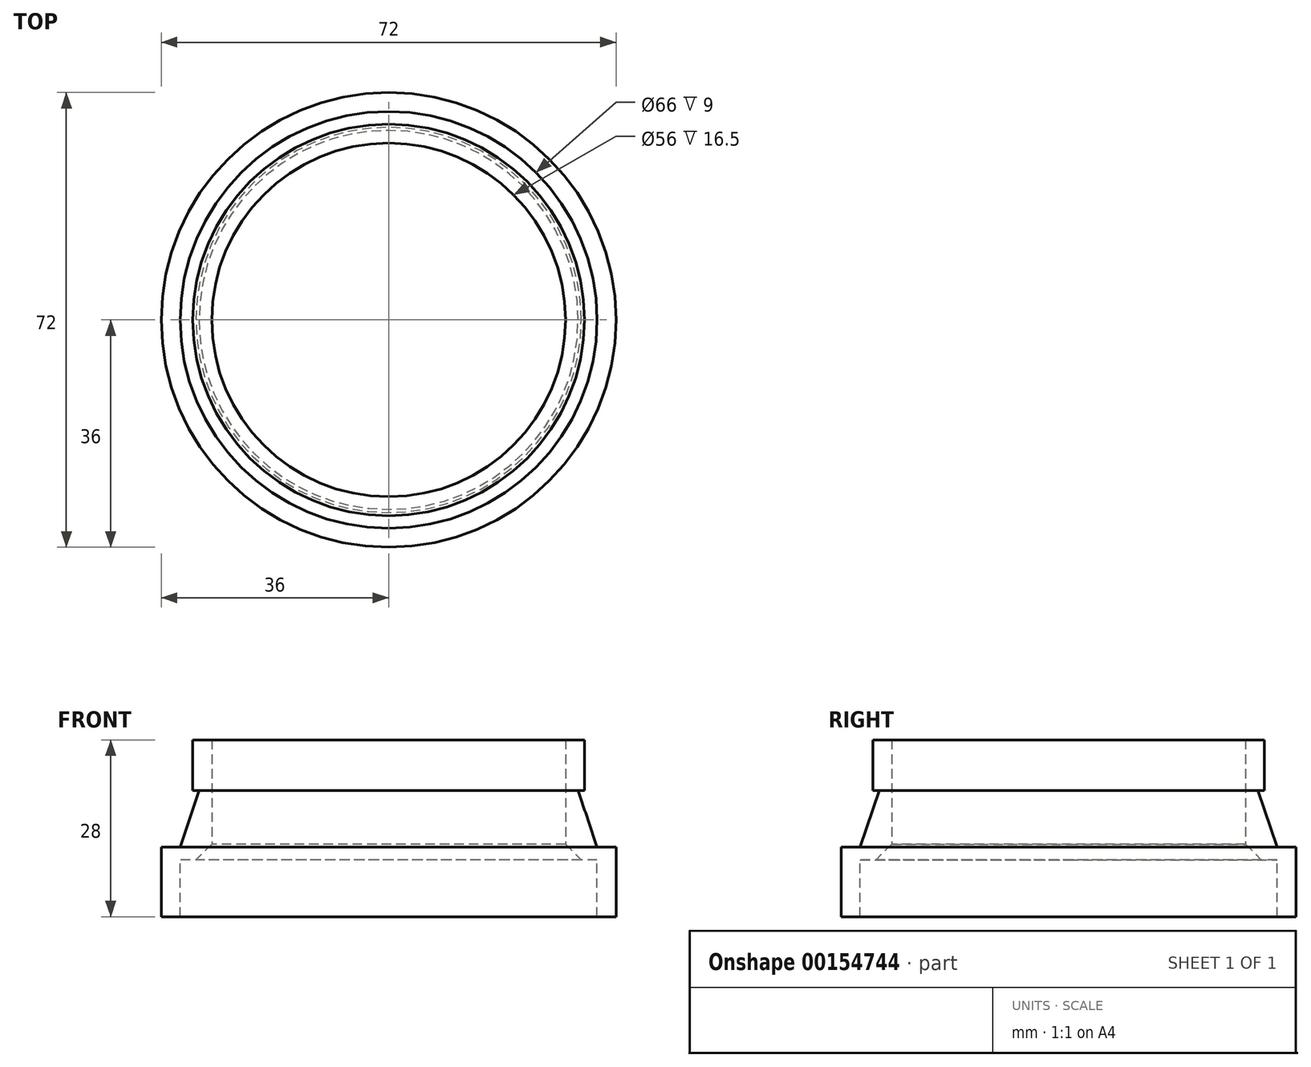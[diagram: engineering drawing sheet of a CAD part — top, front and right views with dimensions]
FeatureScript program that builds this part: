
annotation { "Feature Type Name" : "Feature", "Feature Type Description" : "" }
export const myFeature = defineFeature(function(context is Context, id is Id, definition is map)
    precondition{}
    {
        {
            var Q0;
            Q0=qCreatedBy(makeId("Top.planeOp"),FACE);
            var sketch = newSketch(context, id + "F0", { "sketchPlane" : qUnion([Q0])});
            skCircle(sketch, "E0", {"center": v(0, 0) * mm, "radius": 36 * mm});
            skCircle(sketch, "E1", {"center": v(0, 0) * mm, "radius": 28 * mm});
            skSolve(sketch);
        }
        {
            var Q0;
            Q0=makeQuery(id+"F0.imprint","IMPRINT",FACE,{"disambiguationData":[TD([[makeQuery(id+"F0.imprint","IMPRINT",EDGE,{"derivedFrom":sQuery(id+"F0.wireOp",EDGE,"E0")}),1.0]])]});
            extrude(context, id + "F1", {"entities" : qUnion([Q0]), "depth" : 28 * mm});
        }
        {
            var Q0;
            Q0=qCreatedBy(makeId("Front.planeOp"),FACE);
            var sketch = newSketch(context, id + "F2", { "sketchPlane" : qUnion([Q0])});
            skLineSegment(sketch, "E2", {"start": v(36, 28) * mm, "end": v(36, 0) * mm, "construction": true});
            skLineSegment(sketch, "E3", {"start": v(-36, 0) * mm, "end": v(-36, 28) * mm, "construction": true});
            skLineSegment(sketch, "E4.0", {"start": v(-36, 28) * mm, "end": v(36, 28) * mm, "construction": true});
            skLineSegment(sketch, "E5", {"start": v(-28, 0) * mm, "end": v(-28, 28) * mm, "construction": true});
            skLineSegment(sketch, "E6", {"start": v(28, 28) * mm, "end": v(28, 0) * mm, "construction": true});
            skLineSegment(sketch, "E7.0", {"start": v(-36, 0) * mm, "end": v(36, 0) * mm, "construction": true});
            skLineSegment(sketch, "E8", {"start": v(36, 11) * mm, "end": v(33, 11) * mm});
            skLineSegment(sketch, "E9", {"start": v(33, 11) * mm, "end": v(30, 20) * mm});
            skLineSegment(sketch, "E10", {"start": v(30, 20) * mm, "end": v(31, 20) * mm});
            skLineSegment(sketch, "E11", {"start": v(31, 20) * mm, "end": v(31, 28) * mm});
            skLineSegment(sketch, "E12", {"start": v(31, 28) * mm, "end": v(48.8, 33.8) * mm});
            skLineSegment(sketch, "E13", {"start": v(48.8, 33.8) * mm, "end": v(49.78, 8.36) * mm});
            skLineSegment(sketch, "E14", {"start": v(49.78, 8.36) * mm, "end": v(36, 11) * mm});
            skLineSegment(sketch, "E15", {"start": v(33, 0) * mm, "end": v(33, 9) * mm});
            skLineSegment(sketch, "E16", {"start": v(33, 9) * mm, "end": v(30.5, 9) * mm});
            skLineSegment(sketch, "E17", {"start": v(30.5, 9) * mm, "end": v(28, 11.5) * mm});
            skLineSegment(sketch, "E18", {"start": v(28, 11.5) * mm, "end": v(22.76, -1.32) * mm});
            skLineSegment(sketch, "E19", {"start": v(22.76, -1.32) * mm, "end": v(33, 0) * mm});
            skLineSegment(sketch, "E20", {"start": v(0, 0) * mm, "end": v(0, 28) * mm, "construction": true});
            skSolve(sketch);
        }
        {
            var Q0;
            Q0 = qSketchRegion(id + "F2", true);
            var Q1;
            Q1=sQuery(id+"F2.wireOp",EDGE,"E20");
            revolve(context, id + "F3", {"operationType" : NewBodyOperationType.REMOVE, "entities" : qUnion([Q0]), "axis" : qUnion([Q1]), "revolveType" : RevolveType.FULL, "oppositeDirection" : true});
        }
    });
